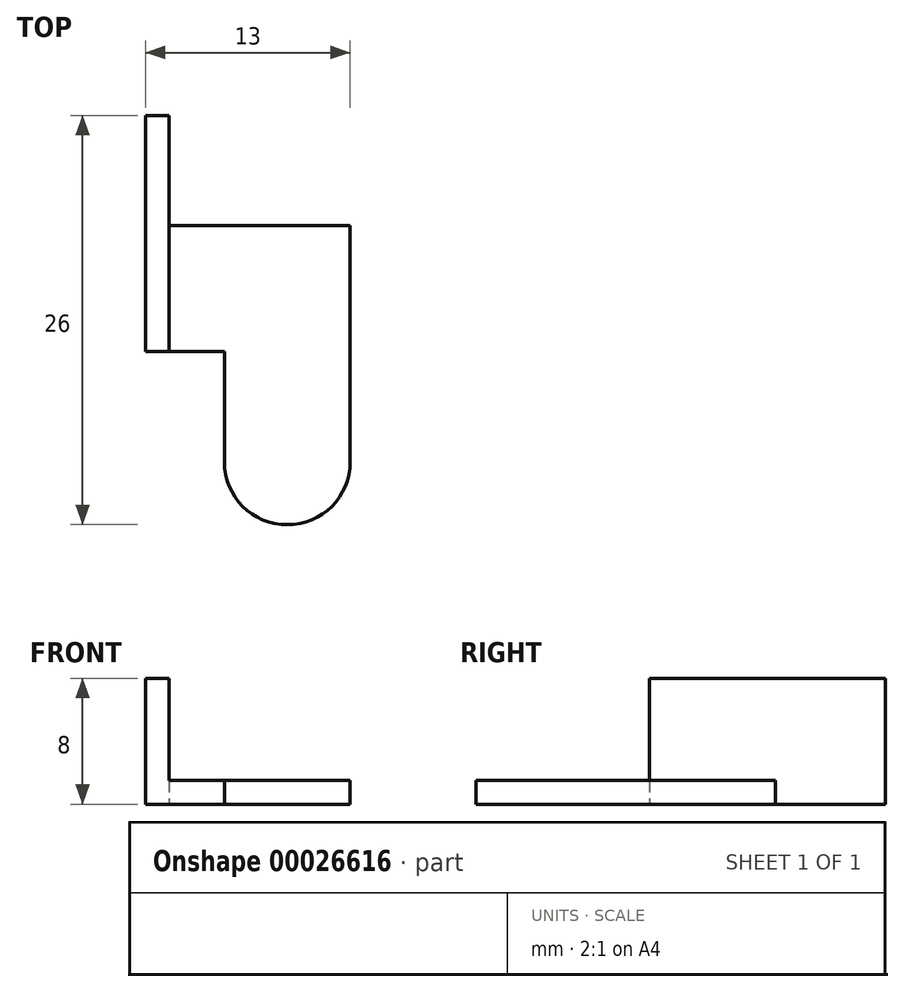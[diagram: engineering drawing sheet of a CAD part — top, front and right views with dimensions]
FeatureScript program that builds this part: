
annotation { "Feature Type Name" : "Feature", "Feature Type Description" : "" }
export const myFeature = defineFeature(function(context is Context, id is Id, definition is map)
    precondition{}
    {
        {
            var Q0;
            Q0=qCreatedBy(makeId("Top.planeOp"),FACE);
            var sketch = newSketch(context, id + "F0", { "sketchPlane" : qUnion([Q0])});
            skLineSegment(sketch, "E0", {"start": v(0, 4) * mm, "end": v(0, 11) * mm});
            skLineSegment(sketch, "E1", {"start": v(0, 11) * mm, "end": v(-5, 11) * mm});
            skLineSegment(sketch, "E2", {"start": v(-5, 11) * mm, "end": v(-5, 19) * mm});
            skLineSegment(sketch, "E3", {"start": v(-5, 19) * mm, "end": v(8, 19) * mm});
            skLineSegment(sketch, "E4", {"start": v(8, 19) * mm, "end": v(8, 4) * mm});
            skLineSegment(sketch, "E5", {"start": v(4, 0) * mm, "end": v(4, 19) * mm, "construction": true});
            skCircle(sketch, "E6", {"center": v(4, 4) * mm, "radius": 4 * mm});
            skPoint(sketch, "E7.orphan", {"position": v(8, 0) * mm});
            skPoint(sketch, "E8.orphan", {"position": v(0, 0) * mm});
            skLineSegment(sketch, "E9", {"start": v(4, 19) * mm, "end": v(4, 22.24) * mm, "construction": true});
            skLineSegment(sketch, "E10", {"start": v(4, 22.24) * mm, "end": v(-5, 22.24) * mm, "construction": true});
            skLineSegment(sketch, "E11", {"start": v(-5, 22.24) * mm, "end": v(-5, 19) * mm, "construction": true});
            skSolve(sketch);
        }
        {
            var Q0;
            Q0 = qSketchRegion(id + "F0", true);
            extrude(context, id + "F1", {"entities" : qUnion([Q0]), "depth" : 1.5 * mm});
        }
        {
            var Q0;
            Q0=makeQuery(id+"F1.opExtrude","SWEPT_FACE",FACE,{"disambiguationData":[OSD([sQuery(id+"F0.wireOp",EDGE,"E3")])]});
            var sketch = newSketch(context, id + "F2", { "sketchPlane" : qUnion([Q0])});
            skLineSegment(sketch, "E12.bottom", {"start": v(5, 0) * mm, "end": v(3.5, 0) * mm});
            skLineSegment(sketch, "E12.top", {"start": v(5, 8) * mm, "end": v(3.5, 8) * mm});
            skLineSegment(sketch, "E12.left", {"start": v(5, 0) * mm, "end": v(5, 8) * mm});
            skLineSegment(sketch, "E12.right", {"start": v(3.5, 0) * mm, "end": v(3.5, 8) * mm});
            skSolve(sketch);
        }
        {
            var Q0;
            Q0 = qSketchRegion(id + "F2", true);
            extrude(context, id + "F3", {"entities" : qUnion([Q0]), "operationType" : NewBodyOperationType.ADD, "depth" : 7 * mm, "hasSecondDirection" : true, "secondDirectionOppositeDirection" : true, "secondDirectionDepth" : 8 * mm});
        }
    });
